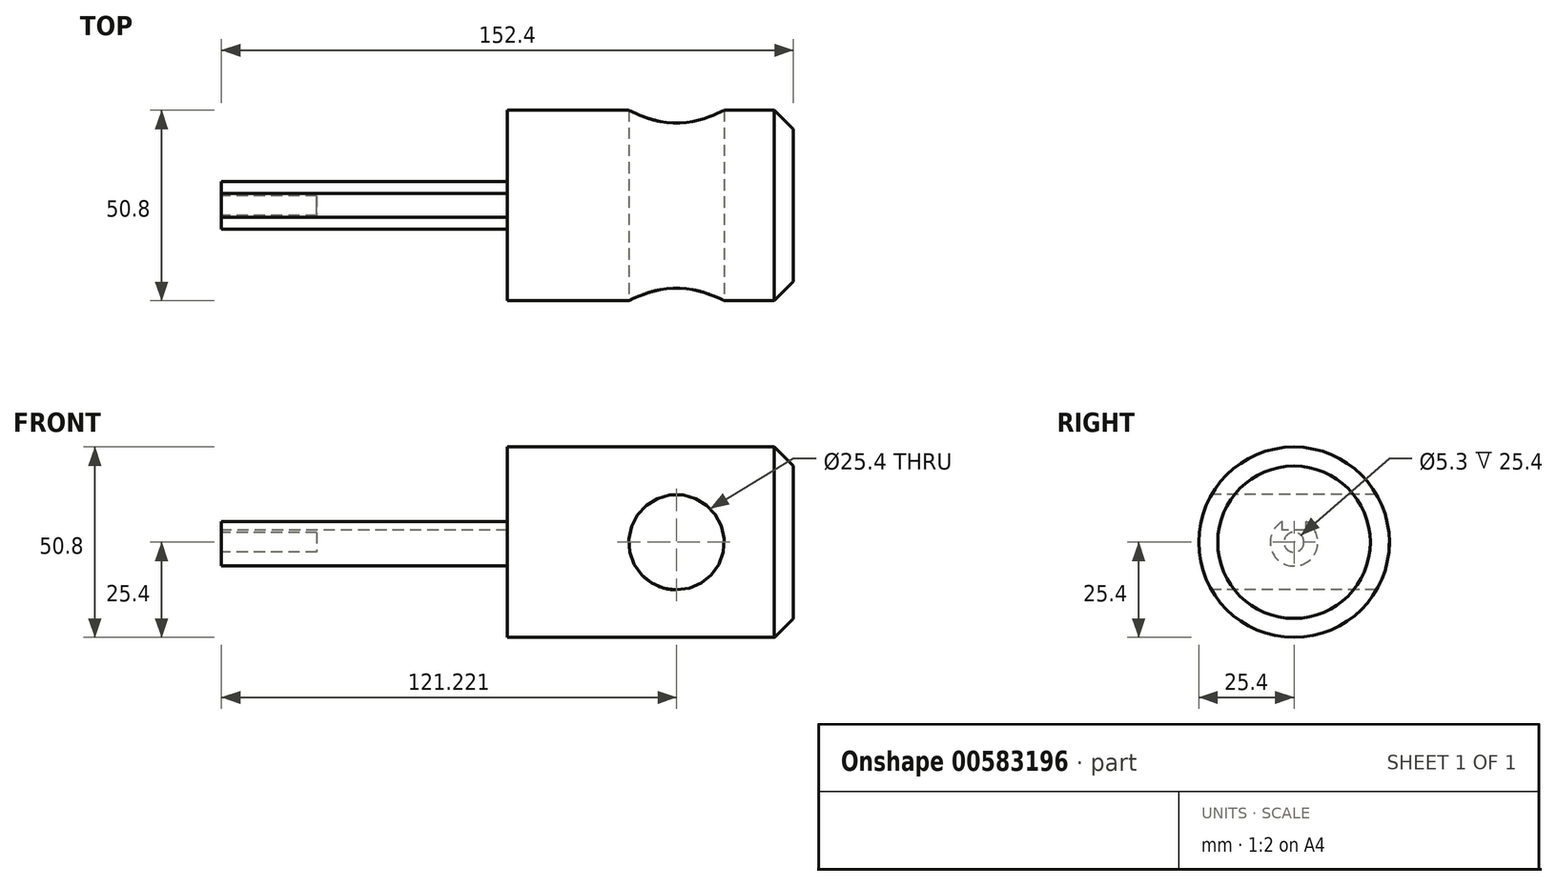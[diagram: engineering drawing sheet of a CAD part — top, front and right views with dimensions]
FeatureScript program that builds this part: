
annotation { "Feature Type Name" : "Feature", "Feature Type Description" : "" }
export const myFeature = defineFeature(function(context is Context, id is Id, definition is map)
    precondition{}
    {
        {
            var Q0;
            Q0=qCreatedBy(makeId("Right.planeOp"),FACE);
            var sketch = newSketch(context, id + "F0", { "sketchPlane" : qUnion([Q0])});
            skArc(sketch, "E0", {"start": v(-3.18, 5.5) * mm, "mid": v(0, -6.35) * mm, "end": v(3.18, 5.5) * mm});
            skLineSegment(sketch, "E1", {"start": v(0, 10.2) * mm, "end": v(0, -9.55) * mm, "construction": true});
            skLineSegment(sketch, "E2", {"start": v(-8.2, 0) * mm, "end": v(7.77, 0) * mm, "construction": true});
            skLineSegment(sketch, "E3.bottom", {"start": v(3.17, 3.17) * mm, "end": v(-3.18, 3.17) * mm});
            skLineSegment(sketch, "E3.top", {"start": v(3.17, 9.53) * mm, "end": v(-3.18, 9.53) * mm});
            skLineSegment(sketch, "E3.left", {"start": v(3.17, 3.17) * mm, "end": v(3.17, 9.53) * mm});
            skLineSegment(sketch, "E3.right", {"start": v(-3.18, 3.17) * mm, "end": v(-3.18, 9.53) * mm});
            skPoint(sketch, "E3.middle", {"position": v(0, 6.35) * mm});
            skSolve(sketch);
        }
        {
            var Q0;
            {var subQ0=sQuery(id+"F0.wireOp",EDGE,"E0");Q0=makeQuery(id+"F0.imprint","IMPRINT",FACE,{"disambiguationData":[TD([[makeQuery(id+"F0.imprint","IMPRINT",EDGE,{"derivedFrom":subQ0}),1.0]])]});}
            extrude(context, id + "F1", {"entities" : qUnion([Q0]), "depth" : 76.2 * mm, "offsetDistance" : 25.4 * mm});
        }
        {
            var Q0;
            Q0=makeQuery(id+"F1.opExtrude","CAP_FACE",FACE,{"disambiguationData":[OSD([sQuery(id+"F0.wireOp",EDGE,"E0"),sQuery(id+"F0.wireOp",EDGE,"E3.bottom"),sQuery(id+"F0.wireOp",EDGE,"E3.left"),sQuery(id+"F0.wireOp",EDGE,"E3.right")])],"isStart":false});
            var sketch = newSketch(context, id + "F2", { "sketchPlane" : qUnion([Q0])});
            skCircle(sketch, "E4", {"center": v(0, 0) * mm, "radius": 25.4 * mm});
            skSolve(sketch);
        }
        {
            var Q0;
            Q0 = qSketchRegion(id + "F2", true);
            extrude(context, id + "F3", {"entities" : qUnion([Q0]), "operationType" : NewBodyOperationType.ADD, "depth" : 76.2 * mm, "offsetDistance" : 25.4 * mm});
        }
        {
            var Q0;
            Q0=makeQuery(id+"F1.opExtrude","CAP_FACE",FACE,{"disambiguationData":[OSD([sQuery(id+"F0.wireOp",EDGE,"E0"),sQuery(id+"F0.wireOp",EDGE,"E3.bottom"),sQuery(id+"F0.wireOp",EDGE,"E3.left"),sQuery(id+"F0.wireOp",EDGE,"E3.right")])],"isStart":true});
            var sketch = newSketch(context, id + "F4", { "sketchPlane" : qUnion([Q0])});
            skCircle(sketch, "E5", {"center": v(0, 0) * mm, "radius": 2.65 * mm});
            skSolve(sketch);
        }
        {
            var Q0;
            Q0=makeQuery(id+"F4.imprint","IMPRINT",FACE,{"disambiguationData":[TD([[makeQuery(id+"F4.imprint","IMPRINT",EDGE,{"derivedFrom":sQuery(id+"F4.wireOp",EDGE,"E5")}),1.0]])]});
            var Q1;
            Q1=makeQuery(id+"F4.imprint","IMPRINT",FACE,{"disambiguationData":[TD([[makeQuery(id+"F4.imprint","IMPRINT",EDGE,{"derivedFrom":sQuery(id+"F4.wireOp",EDGE,"E5")}),1.0]])]});
            extrude(context, id + "F5", {"entities" : qUnion([Q0, Q1]), "operationType" : NewBodyOperationType.REMOVE, "oppositeDirection" : true, "depth" : 25.4 * mm, "offsetDistance" : 25.4 * mm});
        }
        {
            var Q0;
            Q0=qCreatedBy(makeId("Front.planeOp"),FACE);
            var sketch = newSketch(context, id + "F6", { "sketchPlane" : qUnion([Q0])});
            skCircle(sketch, "E6", {"center": v(121.22, 0) * mm, "radius": 12.7 * mm});
            skSolve(sketch);
        }
        {
            var Q0;
            Q0 = qSketchRegion(id + "F6", true);
            extrude(context, id + "F7", {"entities" : qUnion([Q0]), "operationType" : NewBodyOperationType.REMOVE, "oppositeDirection" : true, "depth" : 50.8 * mm, "offsetDistance" : 25.4 * mm, "symmetric" : true});
        }
        {
            var Q0;
            Q0=makeQuery(id+"F3.opExtrude","CAP_EDGE",EDGE,{"disambiguationData":[OSD([sQuery(id+"F2.wireOp",EDGE,"E4")])],"isStart":false});
            chamfer(context, id + "F8", {"entities" : qUnion([Q0]), "width" : 5.08 * mm, "tangentPropagation" : true});
        }
    });
